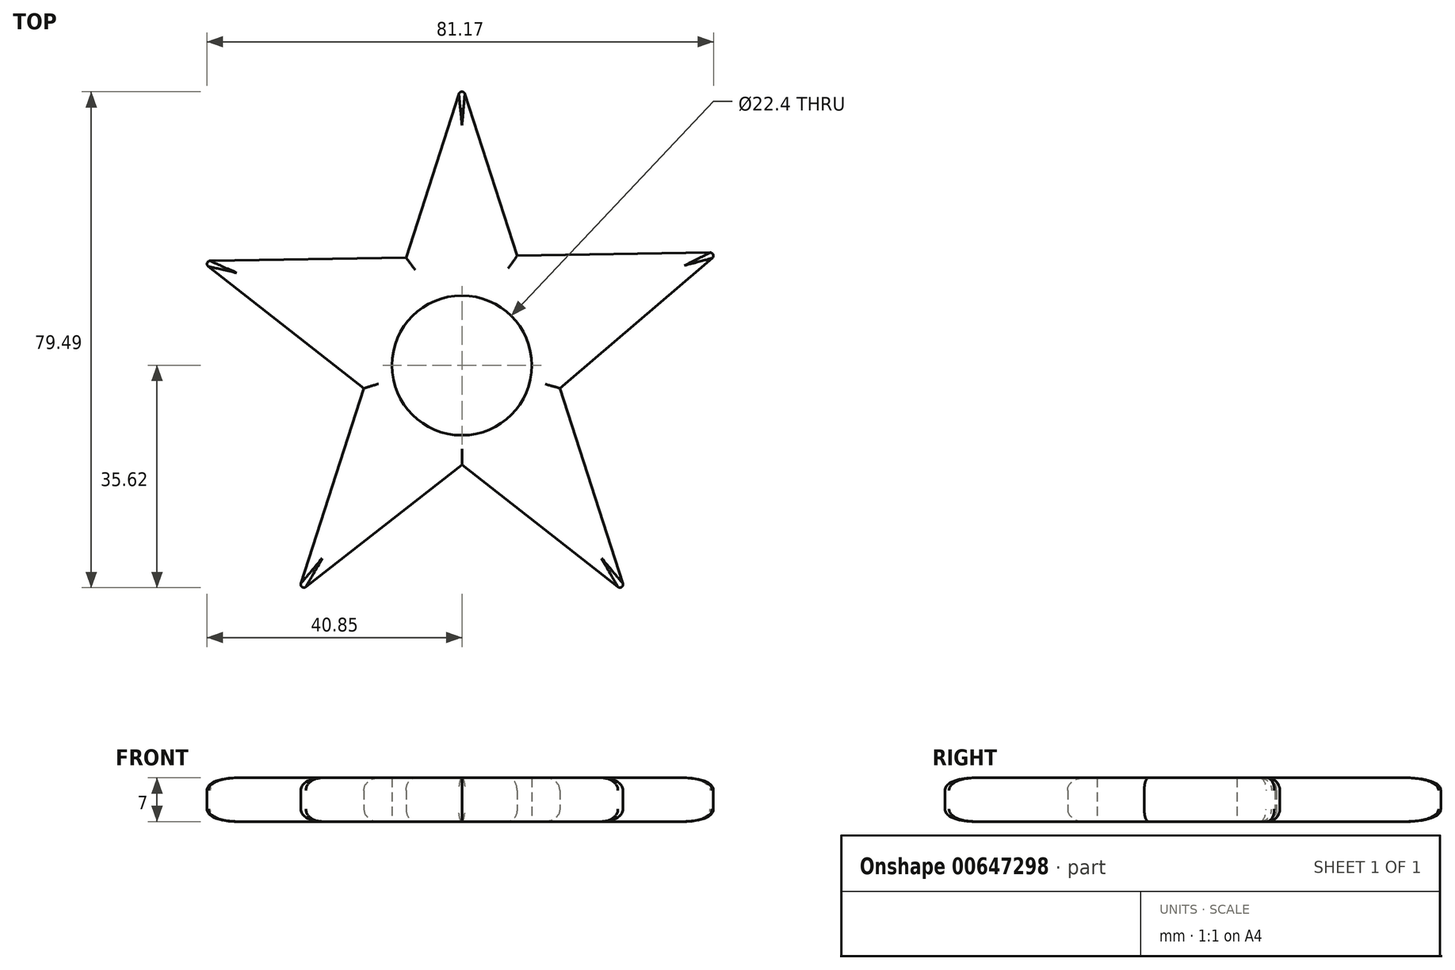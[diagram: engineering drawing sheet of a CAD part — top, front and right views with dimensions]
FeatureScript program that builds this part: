
annotation { "Feature Type Name" : "Feature", "Feature Type Description" : "" }
export const myFeature = defineFeature(function(context is Context, id is Id, definition is map)
    precondition{}
    {
        {
            var Q0;
            Q0=qCreatedBy(makeId("Top.planeOp"),FACE);
            var sketch = newSketch(context, id + "F0", { "sketchPlane" : qUnion([Q0])});
            skCircle(sketch, "E0", {"center": v(0, 0) * mm, "radius": 11.2 * mm});
            skCircle(sketch, "E1", {"center": v(0, 0) * mm, "radius": 45 * mm});
            skLineSegment(sketch, "E2", {"start": v(0, 45) * mm, "end": v(-8.95, 17.27) * mm});
            skLineSegment(sketch, "E3", {"start": v(-8.95, 17.27) * mm, "end": v(-41.77, 16.73) * mm});
            skLineSegment(sketch, "E4", {"start": v(-41.77, 16.73) * mm, "end": v(-15.7, -3.66) * mm});
            skLineSegment(sketch, "E5", {"start": v(-15.7, -3.66) * mm, "end": v(-26.3, -36.52) * mm});
            skLineSegment(sketch, "E6", {"start": v(-26.3, -36.52) * mm, "end": v(0, -15.94) * mm});
            skLineSegment(sketch, "E7", {"start": v(0, -15.94) * mm, "end": v(26.3, -36.52) * mm});
            skLineSegment(sketch, "E8", {"start": v(26.3, -36.52) * mm, "end": v(15.7, -3.66) * mm});
            skLineSegment(sketch, "E9", {"start": v(15.7, -3.66) * mm, "end": v(41.2, 18.1) * mm});
            skLineSegment(sketch, "E10", {"start": v(8.85, 17.57) * mm, "end": v(41.2, 18.1) * mm});
            skLineSegment(sketch, "E11", {"start": v(8.85, 17.57) * mm, "end": v(0, 45) * mm});
            skSolve(sketch);
        }
        {
            var Q0;
            Q0=makeQuery(id+"F0.imprint","IMPRINT",FACE,{"disambiguationData":[TD([[makeQuery(id+"F0.imprint","IMPRINT",EDGE,{"derivedFrom":sQuery(id+"F0.wireOp",EDGE,"E0")}),-1.0]])]});
            extrude(context, id + "F1", {"entities" : qUnion([Q0]), "depth" : 7 * mm, "offsetDistance" : 25.4 * mm});
        }
        {
            var Q0;
            Q0=makeQuery(id+"F1.opExtrude","SWEPT_EDGE",EDGE,{"disambiguationData":[OSD([sQuery(id+"F0.wireOp",EDGE,"E1"),sQuery(id+"F0.wireOp",EDGE,"E3"),sQuery(id+"F0.wireOp",EDGE,"E4")])]});
            var Q1;
            Q1=makeQuery(id+"F1.opExtrude","SWEPT_EDGE",EDGE,{"disambiguationData":[OSD([sQuery(id+"F0.wireOp",EDGE,"E1"),sQuery(id+"F0.wireOp",EDGE,"E2"),sQuery(id+"F0.wireOp",EDGE,"E11")])]});
            var Q2;
            Q2=makeQuery(id+"F1.opExtrude","SWEPT_EDGE",EDGE,{"disambiguationData":[OSD([sQuery(id+"F0.wireOp",EDGE,"E1"),sQuery(id+"F0.wireOp",EDGE,"E9"),sQuery(id+"F0.wireOp",EDGE,"E10")])]});
            var Q3;
            Q3=makeQuery(id+"F1.opExtrude","SWEPT_EDGE",EDGE,{"disambiguationData":[OSD([sQuery(id+"F0.wireOp",EDGE,"E1"),sQuery(id+"F0.wireOp",EDGE,"E7"),sQuery(id+"F0.wireOp",EDGE,"E8")])]});
            var Q4;
            Q4=makeQuery(id+"F1.opExtrude","SWEPT_EDGE",EDGE,{"disambiguationData":[OSD([sQuery(id+"F0.wireOp",EDGE,"E1"),sQuery(id+"F0.wireOp",EDGE,"E5"),sQuery(id+"F0.wireOp",EDGE,"E6")])]});
            fillet(context, id + "F2", {"entities" : qUnion([Q0, Q1, Q2, Q3, Q4]), "radius" : .5 * mm, "tangentPropagation" : true, "allowEdgeOverflow" : false});
        }
        {
            var Q0;
            Q0=makeQuery(id+"F1.opExtrude","CAP_EDGE",EDGE,{"disambiguationData":[OSD([sQuery(id+"F0.wireOp",EDGE,"E3")])],"isStart":false});
            var Q1;
            Q1=makeQuery(id+"F1.opExtrude","CAP_EDGE",EDGE,{"disambiguationData":[OSD([sQuery(id+"F0.wireOp",EDGE,"E2")])],"isStart":false});
            var Q2;
            Q2=makeQuery(id+"F1.opExtrude","CAP_EDGE",EDGE,{"disambiguationData":[OSD([sQuery(id+"F0.wireOp",EDGE,"E10")])],"isStart":false});
            var Q3;
            Q3=makeQuery(id+"F1.opExtrude","CAP_EDGE",EDGE,{"disambiguationData":[OSD([sQuery(id+"F0.wireOp",EDGE,"E8")])],"isStart":false});
            var Q4;
            Q4=makeQuery(id+"F1.opExtrude","CAP_EDGE",EDGE,{"disambiguationData":[OSD([sQuery(id+"F0.wireOp",EDGE,"E6")])],"isStart":false});
            var Q5;
            Q5=makeQuery(id+"F1.opExtrude","CAP_EDGE",EDGE,{"disambiguationData":[OSD([sQuery(id+"F0.wireOp",EDGE,"E5")])],"isStart":true});
            var Q6;
            Q6=makeQuery(id+"F1.opExtrude","CAP_EDGE",EDGE,{"disambiguationData":[OSD([sQuery(id+"F0.wireOp",EDGE,"E4")])],"isStart":true});
            var Q7;
            Q7=makeQuery(id+"F1.opExtrude","CAP_EDGE",EDGE,{"disambiguationData":[OSD([sQuery(id+"F0.wireOp",EDGE,"E3")])],"isStart":true});
            var Q8;
            Q8=makeQuery(id+"F1.opExtrude","CAP_EDGE",EDGE,{"disambiguationData":[OSD([sQuery(id+"F0.wireOp",EDGE,"E2")])],"isStart":true});
            var Q9;
            Q9=makeQuery(id+"F1.opExtrude","CAP_EDGE",EDGE,{"disambiguationData":[OSD([sQuery(id+"F0.wireOp",EDGE,"E11")])],"isStart":true});
            var Q10;
            Q10=makeQuery(id+"F1.opExtrude","CAP_EDGE",EDGE,{"disambiguationData":[OSD([sQuery(id+"F0.wireOp",EDGE,"E10")])],"isStart":true});
            var Q11;
            Q11=makeQuery(id+"F1.opExtrude","CAP_EDGE",EDGE,{"disambiguationData":[OSD([sQuery(id+"F0.wireOp",EDGE,"E9")])],"isStart":true});
            var Q12;
            Q12=makeQuery(id+"F1.opExtrude","CAP_EDGE",EDGE,{"disambiguationData":[OSD([sQuery(id+"F0.wireOp",EDGE,"E8")])],"isStart":true});
            var Q13;
            Q13=makeQuery(id+"F1.opExtrude","CAP_EDGE",EDGE,{"disambiguationData":[OSD([sQuery(id+"F0.wireOp",EDGE,"E7")])],"isStart":true});
            var Q14;
            Q14=makeQuery(id+"F1.opExtrude","CAP_EDGE",EDGE,{"disambiguationData":[OSD([sQuery(id+"F0.wireOp",EDGE,"E6")])],"isStart":true});
            fillet(context, id + "F3", {"entities" : qUnion([Q0, Q1, Q2, Q3, Q4, Q5, Q6, Q7, Q8, Q9, Q10, Q11, Q12, Q13, Q14]), "radius" : 2 * mm, "tangentPropagation" : true, "allowEdgeOverflow" : false});
        }
    });
